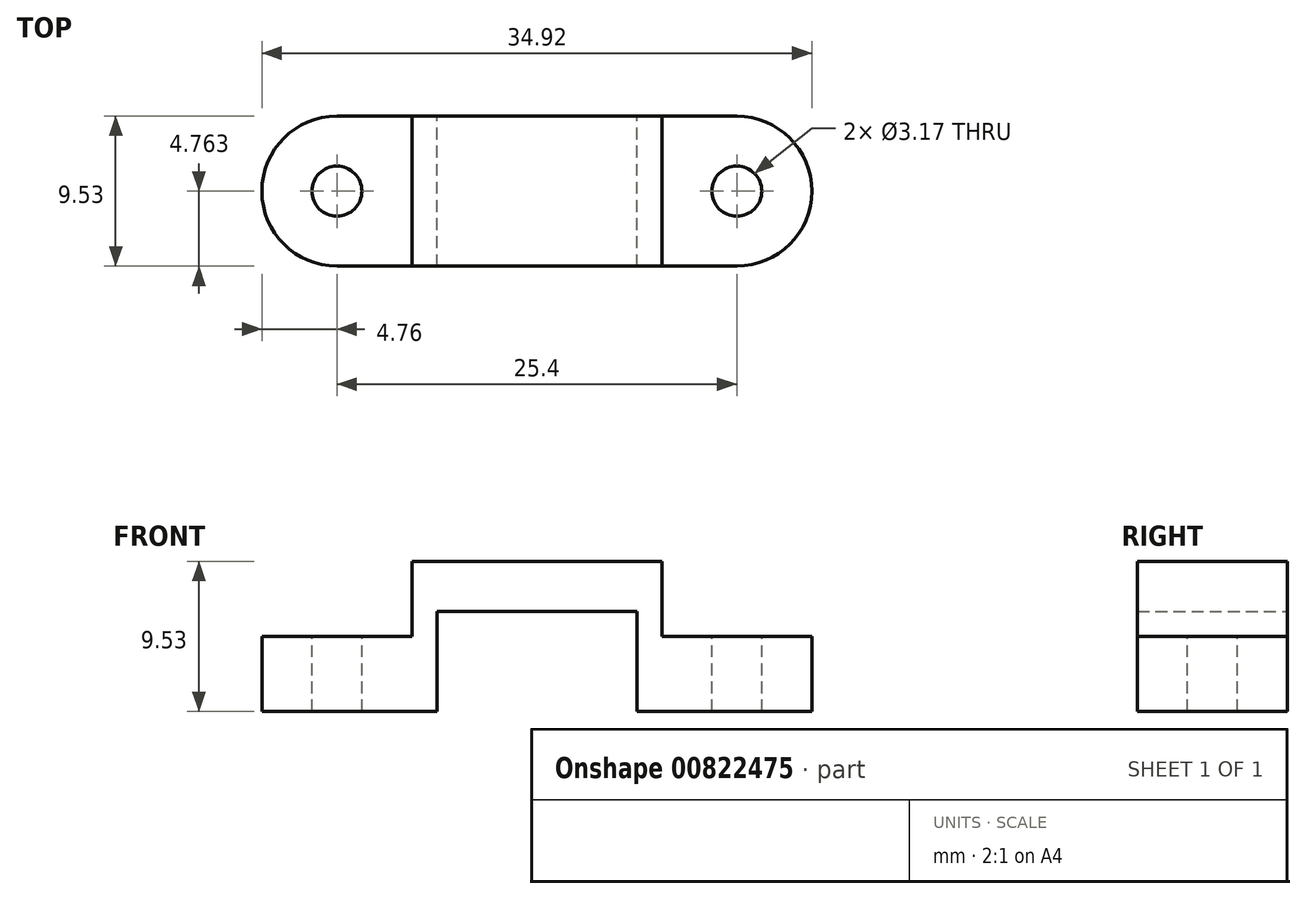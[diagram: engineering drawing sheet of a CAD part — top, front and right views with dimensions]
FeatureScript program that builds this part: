
annotation { "Feature Type Name" : "Feature", "Feature Type Description" : "" }
export const myFeature = defineFeature(function(context is Context, id is Id, definition is map)
    precondition{}
    {
        {
            var Q0;
            Q0=qCreatedBy(makeId("Top.planeOp"),FACE);
            var sketch = newSketch(context, id + "F0", { "sketchPlane" : qUnion([Q0])});
            skLineSegment(sketch, "E0.bottom", {"start": v(0, 0) * mm, "end": v(25.4, 0) * mm});
            skLineSegment(sketch, "E0.top", {"start": v(0, 9.53) * mm, "end": v(25.4, 9.53) * mm});
            skArc(sketch, "E1", {"start": v(25.4, 0) * mm, "mid": v(30.16, 4.76) * mm, "end": v(25.4, 9.53) * mm});
            skArc(sketch, "E2", {"start": v(0, 9.53) * mm, "mid": v(-4.76, 4.76) * mm, "end": v(0, 0) * mm});
            skSolve(sketch);
        }
        {
            var Q0;
            Q0=makeQuery(id+"F0.imprint","IMPRINT",FACE,{"disambiguationData":[TD([[makeQuery(id+"F0.imprint","IMPRINT",EDGE,{"derivedFrom":sQuery(id+"F0.wireOp",EDGE,"E0.bottom")}),1.0]])]});
            extrude(context, id + "F1", {"entities" : qUnion([Q0]), "depth" : 9.52 * mm, "offsetDistance" : 25.4 * mm});
        }
        {
            var Q0;
            Q0=makeQuery(id+"F1.opExtrude","CAP_FACE",FACE,{"disambiguationData":[OSD([sQuery(id+"F0.wireOp",EDGE,"E0.bottom"),sQuery(id+"F0.wireOp",EDGE,"E0.top"),sQuery(id+"F0.wireOp",EDGE,"E0.left"),sQuery(id+"F0.wireOp",EDGE,"E0.right")])],"isStart":true});
            var sketch = newSketch(context, id + "F2", { "sketchPlane" : qUnion([Q0])});
            skLineSegment(sketch, "E3.bottom", {"start": v(6.35, 0) * mm, "end": v(19.05, 0) * mm});
            skLineSegment(sketch, "E3.top", {"start": v(6.35, -9.53) * mm, "end": v(19.05, -9.53) * mm});
            skLineSegment(sketch, "E3.left", {"start": v(6.35, 0) * mm, "end": v(6.35, -9.53) * mm});
            skLineSegment(sketch, "E3.right", {"start": v(19.05, 0) * mm, "end": v(19.05, -9.53) * mm});
            skSolve(sketch);
        }
        {
            var Q0;
            Q0=makeQuery(id+"F2.imprint","IMPRINT",FACE,{"disambiguationData":[TD([[makeQuery(id+"F2.imprint","IMPRINT",EDGE,{"derivedFrom":sQuery(id+"F2.wireOp",EDGE,"E3.bottom")}),-1.0]])]});
            extrude(context, id + "F3", {"entities" : qUnion([Q0]), "operationType" : NewBodyOperationType.REMOVE, "oppositeDirection" : true, "depth" : 6.35 * mm, "offsetDistance" : 25.4 * mm});
        }
        {
            var Q0;
            Q0=makeQuery(id+"F1.opExtrude","CAP_FACE",FACE,{"disambiguationData":[OSD([sQuery(id+"F0.wireOp",EDGE,"E0.bottom"),sQuery(id+"F0.wireOp",EDGE,"E0.top"),sQuery(id+"F0.wireOp",EDGE,"E0.left"),sQuery(id+"F0.wireOp",EDGE,"E0.right")])],"isStart":false});
            var sketch = newSketch(context, id + "F4", { "sketchPlane" : qUnion([Q0])});
            skLineSegment(sketch, "E4.bottom", {"start": v(0, 9.53) * mm, "end": v(4.76, 9.53) * mm});
            skLineSegment(sketch, "E4.top", {"start": v(0, 0) * mm, "end": v(4.76, 0) * mm});
            skLineSegment(sketch, "E4.right", {"start": v(4.76, 9.53) * mm, "end": v(4.76, 0) * mm});
            skArc(sketch, "E5", {"start": v(0, 9.53) * mm, "mid": v(-4.76, 4.76) * mm, "end": v(0, 0) * mm});
            skLineSegment(sketch, "E6.bottom", {"start": v(25.4, 9.53) * mm, "end": v(20.64, 9.53) * mm});
            skLineSegment(sketch, "E6.top", {"start": v(25.4, 0) * mm, "end": v(20.64, 0) * mm});
            skLineSegment(sketch, "E6.right", {"start": v(20.64, 9.53) * mm, "end": v(20.64, 0) * mm});
            skArc(sketch, "E7", {"start": v(25.4, 0) * mm, "mid": v(30.16, 4.76) * mm, "end": v(25.4, 9.53) * mm});
            skSolve(sketch);
        }
        {
            var Q0;
            Q0=makeQuery(id+"F4.imprint","IMPRINT",FACE,{"disambiguationData":[TD([[makeQuery(id+"F4.imprint","IMPRINT",EDGE,{"derivedFrom":sQuery(id+"F4.wireOp",EDGE,"E4.bottom")}),-1.0]])]});
            var Q1;
            Q1=makeQuery(id+"F4.imprint","IMPRINT",FACE,{"disambiguationData":[TD([[makeQuery(id+"F4.imprint","IMPRINT",EDGE,{"derivedFrom":sQuery(id+"F4.wireOp",EDGE,"vkijFdiQ-K0wo-75rC-FNiI-y13BS5MP63gj.bottom")}),1.0]])]});
            var Q2;
            Q2=makeQuery(id+"F4.imprint","IMPRINT",FACE,{"disambiguationData":[TD([[makeQuery(id+"F4.imprint","IMPRINT",EDGE,{"derivedFrom":sQuery(id+"F4.wireOp",EDGE,"E6.bottom")}),-1.0]])]});
            extrude(context, id + "F5", {"entities" : qUnion([Q0, Q1, Q2]), "operationType" : NewBodyOperationType.REMOVE, "oppositeDirection" : true, "depth" : 4.76 * mm, "offsetDistance" : 25.4 * mm});
        }
        {
            var Q0;
            Q0=makeQuery(id+"F5.boolean.opBoolean","COPY",FACE,{"derivedFrom":makeQuery(id+"F5.opExtrude","CAP_FACE",FACE,{"disambiguationData":[OSD([sQuery(id+"F4.wireOp",EDGE,"E6.bottom"),sQuery(id+"F4.wireOp",EDGE,"E6.top"),sQuery(id+"F4.wireOp",EDGE,"E6.right"),sQuery(id+"F4.wireOp",EDGE,"E7")])],"isStart":false})});
            var sketch = newSketch(context, id + "F6", { "sketchPlane" : qUnion([Q0])});
            skCircle(sketch, "E8", {"center": v(25.4, 4.76) * mm, "radius": 1.59 * mm});
            skSolve(sketch);
        }
        {
            var Q0;
            Q0=makeQuery(id+"F5.boolean.opBoolean","COPY",FACE,{"derivedFrom":makeQuery(id+"F5.opExtrude","CAP_FACE",FACE,{"disambiguationData":[OSD([sQuery(id+"F4.wireOp",EDGE,"E4.bottom"),sQuery(id+"F4.wireOp",EDGE,"E4.top"),sQuery(id+"F4.wireOp",EDGE,"E4.right"),sQuery(id+"F4.wireOp",EDGE,"E5")])],"isStart":false})});
            var sketch = newSketch(context, id + "F7", { "sketchPlane" : qUnion([Q0])});
            skCircle(sketch, "E9", {"center": v(0, 4.76) * mm, "radius": 1.59 * mm});
            skSolve(sketch);
        }
        {
            var Q0;
            Q0=makeQuery(id+"F7.imprint","IMPRINT",FACE,{"disambiguationData":[TD([[makeQuery(id+"F7.imprint","IMPRINT",EDGE,{"derivedFrom":sQuery(id+"F7.wireOp",EDGE,"E9")}),1.0]])]});
            var Q1;
            Q1=makeQuery(id+"F6.imprint","IMPRINT",FACE,{"disambiguationData":[TD([[makeQuery(id+"F6.imprint","IMPRINT",EDGE,{"derivedFrom":sQuery(id+"F6.wireOp",EDGE,"E8")}),1.0]])]});
            extrude(context, id + "F8", {"entities" : qUnion([Q0, Q1]), "operationType" : NewBodyOperationType.REMOVE, "oppositeDirection" : true, "depth" : 25.4 * mm, "offsetDistance" : 25.4 * mm});
        }
    });
